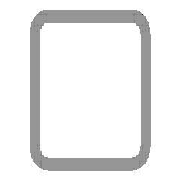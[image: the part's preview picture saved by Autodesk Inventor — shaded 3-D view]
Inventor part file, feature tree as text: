
AUTODESK INVENTOR PART (.ipt)
format: ipt  version: 2022 (Build 260153000, 153)  size: 264,192 bytes
history: native  units: mm (DEFAULTED — no unit token found)
features: other x7, sketch x3, surface_op x2, plane x1
ambient origin geometry x8: Origin, YZ Plane, XZ Plane, XY Plane, X Axis, Y Axis, Z Axis, Center Point
bodies: Body (feature_tree), Solid6 (feature_tree)
feature tree (13):
  parser-record x1  (decoder bookkeeping rows leaked as tree rows — omitted from the tree; the rows remain in map.json)
  other  "Driven Length"
  other  "Start Plane"
  other  "End Plane"
  sketch  "Sketch"  dims[d7=8.0mm d9=40.0mm d11=40.0mm d12=4.0mm d13=-0.0mm d14=180.0mm d15=20.0mm d16=20.0mm d17=90.0deg d18=180.0mm d91=5.0mm d92=5.0mm d93=5.0mm d94=5.0mm d95=5.0mm d96=5.0mm d97=5.0mm d98=5.0mm d99=0.0mm d100=5.0mm d101=5.0mm d102=5.0mm d103=5.0mm d104=5.0mm d105=5.0mm d106=5.0mm d107=5.0mm d108=0.0mm]
  sketch  "Sketch3"  dims[d3=155.0mm]
  plane  "Work Plane3"
  sketch  "Sketch4"  dims[d4=0.0mm]
  other  "Srf14"
  other  "Srf15"
  other  "Srf13"
  surface_op  "Boundary Patch9"
  surface_op  "Boundary Patch10"
